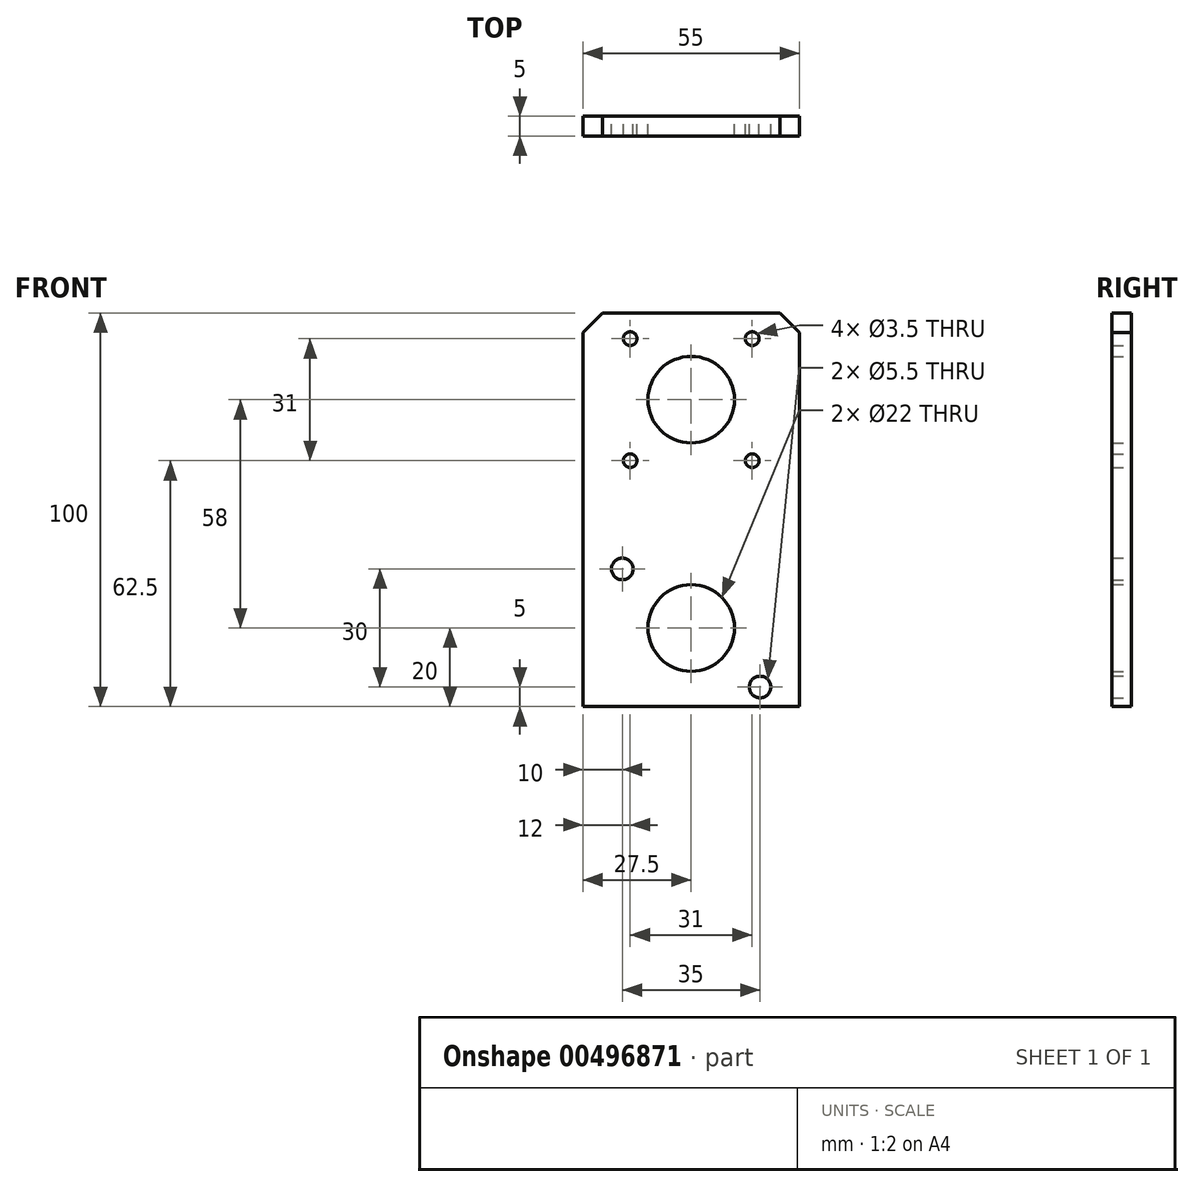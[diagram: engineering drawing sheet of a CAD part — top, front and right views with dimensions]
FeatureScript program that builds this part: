
annotation { "Feature Type Name" : "Feature", "Feature Type Description" : "" }
export const myFeature = defineFeature(function(context is Context, id is Id, definition is map)
    precondition{}
    {
        {
            var Q0;
            Q0=qCreatedBy(makeId("Front.planeOp"),FACE);
            var sketch = newSketch(context, id + "F0", { "sketchPlane" : qUnion([Q0])});
            skLineSegment(sketch, "E0.bottom", {"start": v(27.5, 50) * mm, "end": v(-27.5, 50) * mm});
            skLineSegment(sketch, "E0.top", {"start": v(27.5, -50) * mm, "end": v(-27.5, -50) * mm});
            skLineSegment(sketch, "E0.left", {"start": v(27.5, 50) * mm, "end": v(27.5, -50) * mm});
            skLineSegment(sketch, "E0.right", {"start": v(-27.5, 50) * mm, "end": v(-27.5, -50) * mm});
            skPoint(sketch, "E0.middle", {"position": v(0, 0) * mm});
            skCircle(sketch, "E1", {"center": v(0, 28) * mm, "radius": 11 * mm});
            skCircle(sketch, "E2", {"center": v(15.5, 43.5) * mm, "radius": 1.75 * mm});
            skCircle(sketch, "E3", {"center": v(-15.5, 43.5) * mm, "radius": 1.75 * mm});
            skCircle(sketch, "E4", {"center": v(-15.5, 12.5) * mm, "radius": 1.75 * mm});
            skCircle(sketch, "E5", {"center": v(15.5, 12.5) * mm, "radius": 1.75 * mm});
            skCircle(sketch, "E6", {"center": v(17.5, -45) * mm, "radius": 2.75 * mm});
            skCircle(sketch, "E7", {"center": v(-17.5, -15) * mm, "radius": 2.75 * mm});
            skCircle(sketch, "E8", {"center": v(0, -30) * mm, "radius": 11 * mm});
            skSolve(sketch);
        }
        {
            var Q0;
            Q0 = qSketchRegion(id + "F0", true);
            extrude(context, id + "F1", {"entities" : qUnion([Q0]), "depth" : 5 * mm});
        }
        {
            var Q0;
            Q0=makeQuery(id+"F1.opExtrude","SWEPT_EDGE",EDGE,{"disambiguationData":[OSD([sQuery(id+"F0.wireOp",EDGE,"E0.bottom"),sQuery(id+"F0.wireOp",EDGE,"E0.right")])]});
            chamfer(context, id + "F2", {"entities" : qUnion([Q0]), "width" : 5 * mm, "tangentPropagation" : true});
        }
        {
            var Q0;
            Q0=makeQuery(id+"F1.opExtrude","SWEPT_EDGE",EDGE,{"disambiguationData":[OSD([sQuery(id+"F0.wireOp",EDGE,"E0.bottom"),sQuery(id+"F0.wireOp",EDGE,"E0.left")])]});
            chamfer(context, id + "F3", {"entities" : qUnion([Q0]), "width" : 5 * mm, "tangentPropagation" : true});
        }
    });
